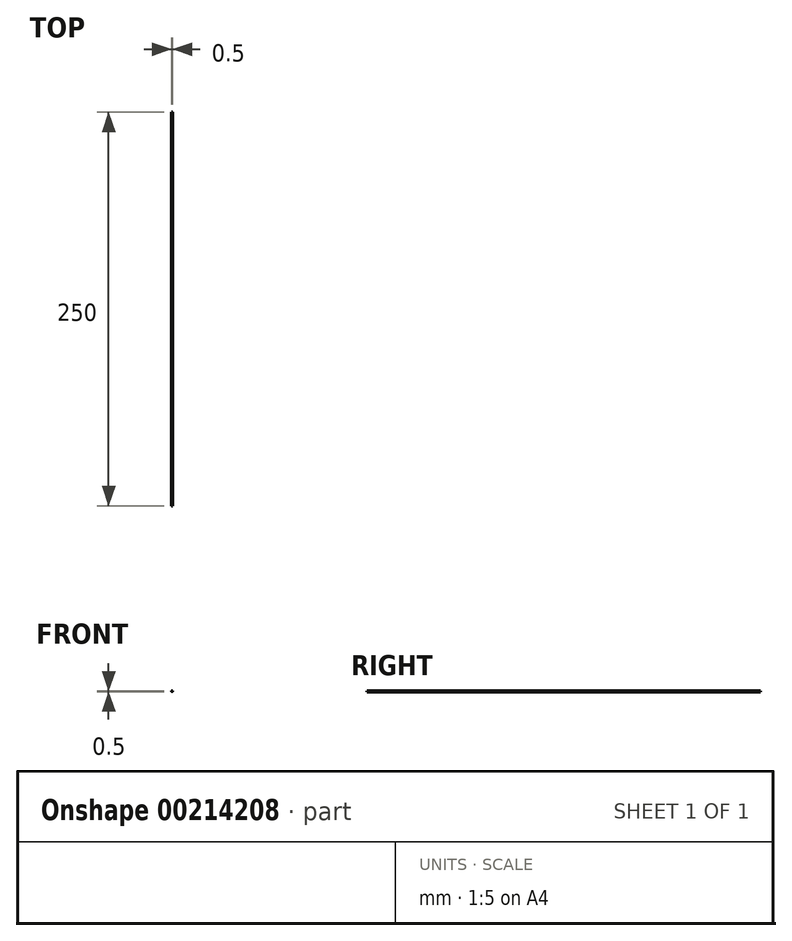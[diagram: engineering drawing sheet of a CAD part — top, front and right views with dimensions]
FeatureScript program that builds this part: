
annotation { "Feature Type Name" : "Feature", "Feature Type Description" : "" }
export const myFeature = defineFeature(function(context is Context, id is Id, definition is map)
    precondition{}
    {
        {
            var Q0;
            Q0=qCreatedBy(makeId("Front.planeOp"),FACE);
            var sketch = newSketch(context, id + "F0", { "sketchPlane" : qUnion([Q0])});
            skCircle(sketch, "E0", {"center": v(0, 0) * mm, "radius": 0.25 * mm});
            skSolve(sketch);
        }
        {
            var Q0;
            Q0 = qSketchRegion(id + "F0", true);
            extrude(context, id + "F1", {"entities" : qUnion([Q0]), "depth" : 250 * mm});
        }
    });
